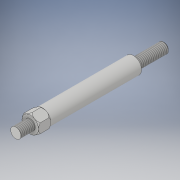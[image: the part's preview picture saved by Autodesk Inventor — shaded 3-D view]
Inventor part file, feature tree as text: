
AUTODESK INVENTOR PART (.ipt)
format: ipt  version: 2018 (Build 220112000, 112)  size: 157,696 bytes
history: native  units: mm
features: sketch x4, extrude x4, thread x2, revolve x1
ambient origin geometry x8: Origin, YZ Plane, XZ Plane, XY Plane, X Axis, Y Axis, Z Axis, Center Point
bodies: Solid1 (feature_tree)
feature tree (11):
  sketch  "Sketch1"  dims[d0=8.0mm d1=6.0mm d2=0.0mm]
  extrude  "Extrusion1"  Depth=6.0mm TaperAngle=0.0deg
  extrude  "Extrusion2"  Depth=6.0mm
  extrude  "Extrusion3"  Depth=2.5mm
  revolve  "Revolution1"  [1 undecoded]
  extrude  "Extrusion4"  Depth=10.0mm
  thread  "Thread1"  [1 undecoded]
  thread  "Thread2"  [1 undecoded]
  sketch  "Sketch2"  dims[d3=6.0mm d4=6.108652mm d5=6.0mm d6=6.108652mm]
  sketch  "Sketch3"  dims[d7=4.0mm d8=2.5mm]
  sketch  "Sketch4"  dims[d9=44.0mm d10=15.0mm d11=0.5mm d12=0.5mm d13=90.0deg d14=5.0mm d15=7.0mm d16=0.0mm d17=10.0mm d18=0.0mm d19=10.0mm d20=0.0mm]
note: 3 required parameter values undecoded (feature->parameter linkage not recoverable at this tier; creation-order binding heuristic only, values carry confidence <= 0.55)